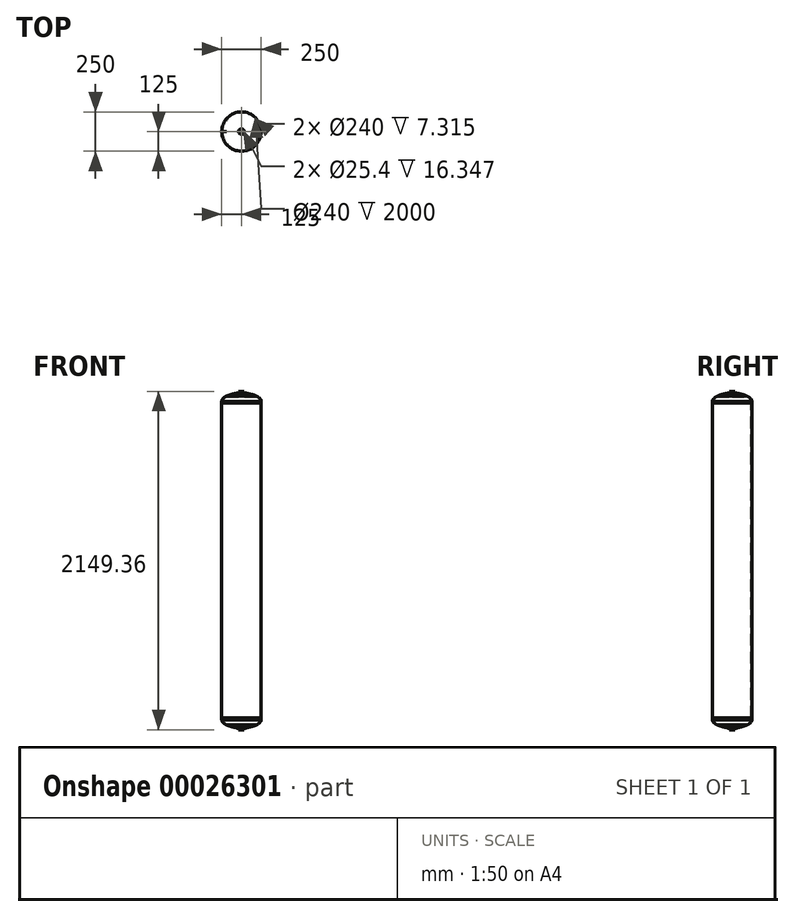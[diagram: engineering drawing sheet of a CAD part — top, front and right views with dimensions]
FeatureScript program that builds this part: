
annotation { "Feature Type Name" : "Feature", "Feature Type Description" : "" }
export const myFeature = defineFeature(function(context is Context, id is Id, definition is map)
    precondition{}
    {
        {
            var Q0;
            Q0=qCreatedBy(makeId("Top.planeOp"),FACE);
            var sketch = newSketch(context, id + "F0", { "sketchPlane" : qUnion([Q0])});
            skCircle(sketch, "E0", {"center": v(0, 0) * mm, "radius": 125 * mm});
            skPoint(sketch, "E1", {"position": v(-125, 0) * mm});
            skPoint(sketch, "E2", {"position": v(125, 0) * mm});
            skSolve(sketch);
        }
        {
            var Q0;
            Q0=qCreatedBy(makeId("Front.planeOp"),FACE);
            var sketch = newSketch(context, id + "F1", { "sketchPlane" : qUnion([Q0])});
            skLineSegment(sketch, "E3", {"start": v(-17.7, 74.68) * mm, "end": v(-17.7, 66.12) * mm});
            skFitSpline(sketch, "E4", {"points": [v(-17.7, 66.12) * mm, v(-94.6, 44.72) * mm, v(-125, 11.34) * mm], "startDerivative": vector(-134.8, -32.11) * mm, "endDerivative": vector(0, -101.43) * mm});
            skLineSegment(sketch, "E5", {"start": v(-125, 0) * mm, "end": v(-125, 11.34) * mm});
            skLineSegment(sketch, "E6", {"start": v(0, -71.97) * mm, "end": v(0, 86.94) * mm, "construction": true});
            skLineSegment(sketch, "E7.2", {"start": v(-12.7, 74.68) * mm, "end": v(-12.7, 58.33) * mm});
            skFitSpline(sketch, "E8", {"points": [v(-12.7, 58.33) * mm, v(-94.6, 39.72) * mm, v(-120, 7.31) * mm], "startDerivative": vector(-139.5, -26.6) * mm, "endDerivative": vector(0, -89.82) * mm});
            skLineSegment(sketch, "E9", {"start": v(-120, 7.31) * mm, "end": v(-120, 0) * mm});
            skLineSegment(sketch, "E10", {"start": v(-120, 0) * mm, "end": v(-125, 0) * mm});
            skLineSegment(sketch, "E11", {"start": v(-17.7, 74.68) * mm, "end": v(-12.7, 74.68) * mm});
            skLineSegment(sketch, "E12", {"start": v(-94.6, 44.72) * mm, "end": v(-94.6, 39.72) * mm});
            skSolve(sketch);
        }
        {
            var Q0;
            Q0 = qSketchRegion(id + "F1", true);
            var Q1;
            Q1=sQuery(id+"F1.wireOp",EDGE,"E6");
            revolve(context, id + "F2", {"entities" : qUnion([Q0]), "axis" : qUnion([Q1]), "revolveType" : RevolveType.FULL});
        }
        {
            var Q0;
            Q0=makeQuery(id+"F2.opRevolve","SWEPT_FACE",FACE,{"disambiguationData":[OSD([sQuery(id+"F1.wireOp",EDGE,"E10")])]});
            extrude(context, id + "F3", {"entities" : qUnion([Q0]), "depth" : 2000 * mm});
        }
        {
            var Q0;
            Q0=qCreatedBy(makeId("Top.planeOp"),FACE);
            cPlane(context, id + "F4", {"entities" : qUnion([Q0]), "cplaneType" : CPlaneType.OFFSET, "offset" : 1000 * mm, "oppositeDirection" : true, "width" : 150 * mm, "height" : 150 * mm});
        }
        {
            var Q0;
            Q0=makeQuery(id+"F2.opRevolve","SWEPT_BODY",BODY,{"disambiguationData":[OSD([sQuery(id+"F1.wireOp",EDGE,"E3"),sQuery(id+"F1.wireOp",EDGE,"E4"),sQuery(id+"F1.wireOp",EDGE,"E5"),sQuery(id+"F1.wireOp",EDGE,"E7.2"),sQuery(id+"F1.wireOp",EDGE,"E8"),sQuery(id+"F1.wireOp",EDGE,"E9"),sQuery(id+"F1.wireOp",EDGE,"E10"),sQuery(id+"F1.wireOp",EDGE,"E11")])]});
            var Q1;
            Q1=qCreatedBy(id+"F4.planeOp",FACE);
            mirror(context, id + "F5", {"entities" : qUnion([Q0]), "mirrorPlane" : qUnion([Q1])});
        }
    });
